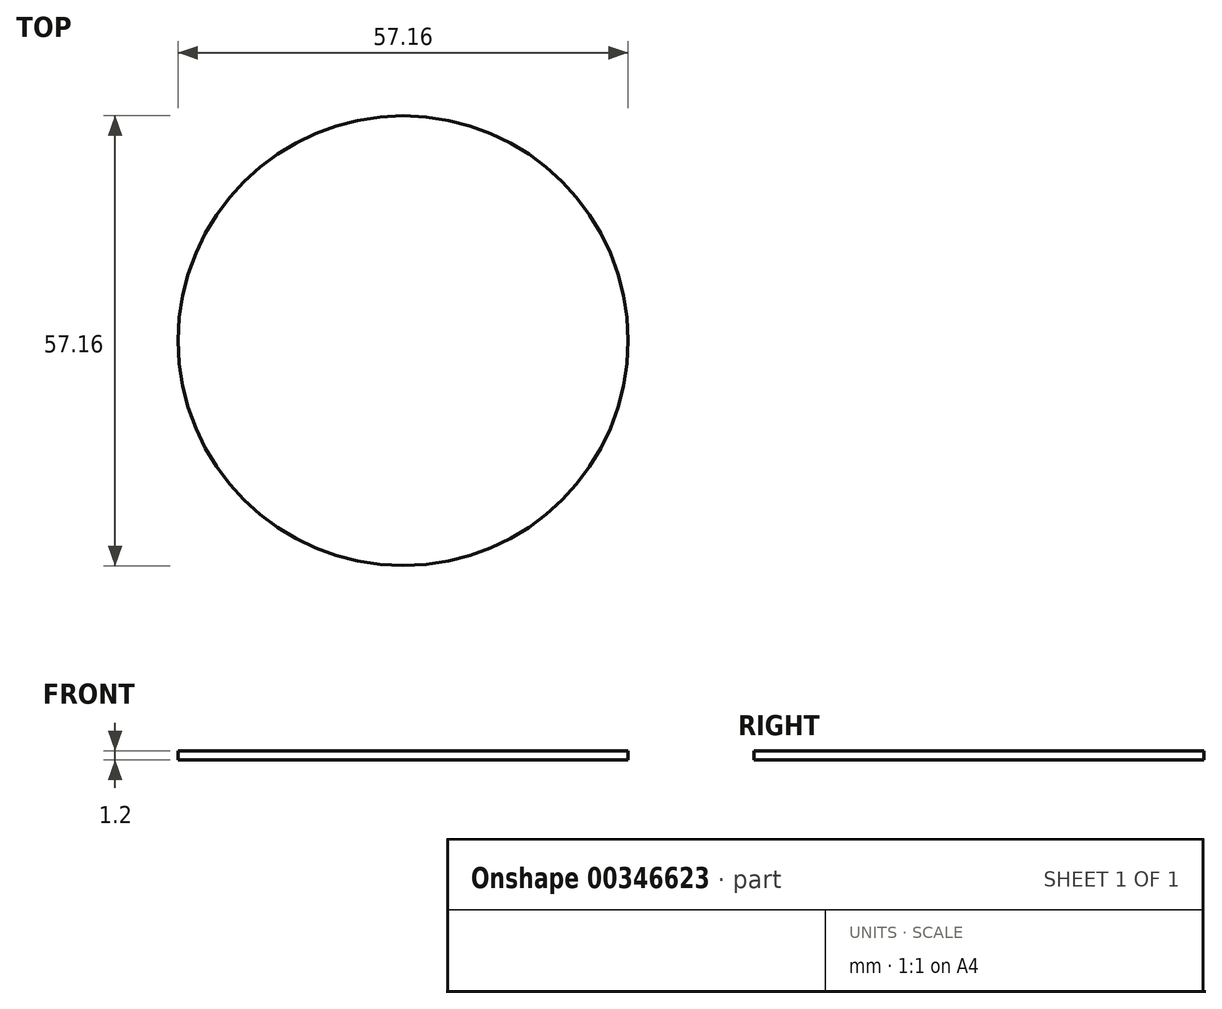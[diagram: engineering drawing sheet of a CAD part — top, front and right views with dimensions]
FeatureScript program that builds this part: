
annotation { "Feature Type Name" : "Feature", "Feature Type Description" : "" }
export const myFeature = defineFeature(function(context is Context, id is Id, definition is map)
    precondition{}
    {
        {
            var Q0;
            Q0=qCreatedBy(makeId("Top.planeOp"),FACE);
            var sketch = newSketch(context, id + "F0", { "sketchPlane" : qUnion([Q0])});
            skCircle(sketch, "E0", {"center": v(0, 0) * mm, "radius": 28.58 * mm});
            skSolve(sketch);
        }
        {
            var Q0;
            Q0 = qSketchRegion(id + "F0", true);
            extrude(context, id + "F1", {"entities" : qUnion([Q0]), "depth" : 1.2 * mm});
        }
    });
